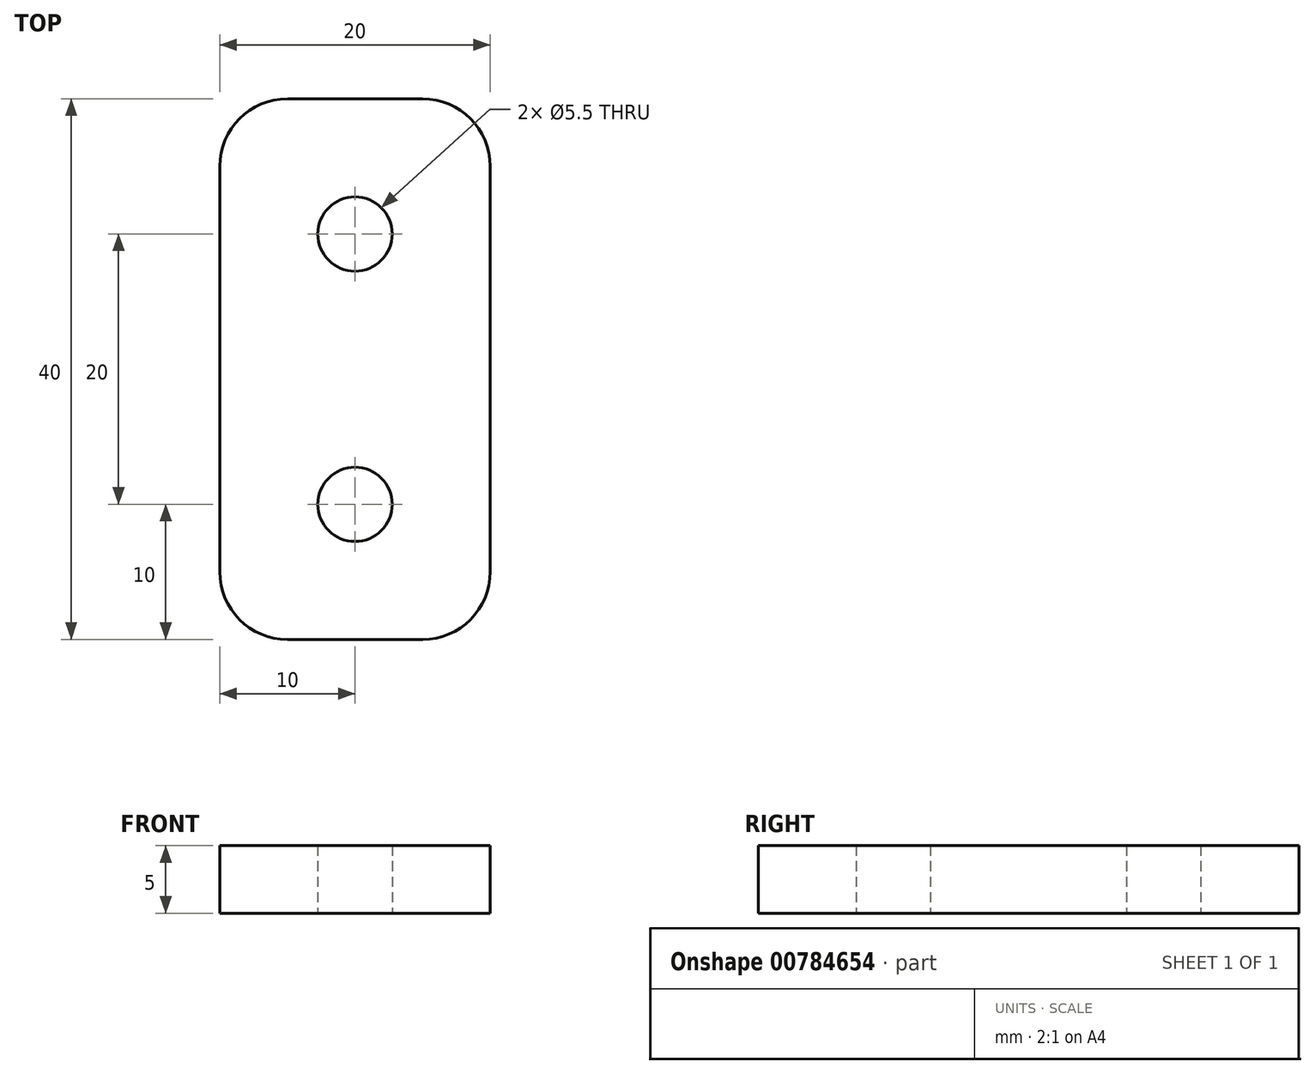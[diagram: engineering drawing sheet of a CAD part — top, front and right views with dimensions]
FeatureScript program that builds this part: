
annotation { "Feature Type Name" : "Feature", "Feature Type Description" : "" }
export const myFeature = defineFeature(function(context is Context, id is Id, definition is map)
    precondition{}
    {
        {
            var Q0;
            Q0=qCreatedBy(makeId("Top.planeOp"),FACE);
            var sketch = newSketch(context, id + "F0", { "sketchPlane" : qUnion([Q0])});
            skCircle(sketch, "E0", {"center": v(0, 10) * mm, "radius": 2.75 * mm});
            skCircle(sketch, "E1", {"center": v(0, -10) * mm, "radius": 2.75 * mm});
            skLineSegment(sketch, "E2.bottom", {"start": v(10, -20) * mm, "end": v(-10, -20) * mm});
            skLineSegment(sketch, "E2.top", {"start": v(10, 20) * mm, "end": v(-10, 20) * mm});
            skLineSegment(sketch, "E2.left", {"start": v(10, -20) * mm, "end": v(10, 20) * mm});
            skLineSegment(sketch, "E2.right", {"start": v(-10, -20) * mm, "end": v(-10, 20) * mm});
            skPoint(sketch, "E2.middle", {"position": v(0, 0) * mm});
            skSolve(sketch);
        }
        {
            var Q0;
            Q0=makeQuery(id+"F0.imprint","IMPRINT",FACE,{"disambiguationData":[TD([[makeQuery(id+"F0.imprint","IMPRINT",EDGE,{"derivedFrom":sQuery(id+"F0.wireOp",EDGE,"E0")}),-1.0]])]});
            extrude(context, id + "F1", {"entities" : qUnion([Q0]), "depth" : 5 * mm, "offsetDistance" : 25 * mm});
        }
        {
            var Q0;
            Q0=makeQuery(id+"F1.opExtrude","SWEPT_EDGE",EDGE,{"disambiguationData":[OSD([sQuery(id+"F0.wireOp",EDGE,"E2.top"),sQuery(id+"F0.wireOp",EDGE,"E2.right")])]});
            var Q1;
            Q1=makeQuery(id+"F1.opExtrude","SWEPT_EDGE",EDGE,{"disambiguationData":[OSD([sQuery(id+"F0.wireOp",EDGE,"E2.top"),sQuery(id+"F0.wireOp",EDGE,"E2.left")])]});
            var Q2;
            Q2=makeQuery(id+"F1.opExtrude","SWEPT_EDGE",EDGE,{"disambiguationData":[OSD([sQuery(id+"F0.wireOp",EDGE,"E2.bottom"),sQuery(id+"F0.wireOp",EDGE,"E2.left")])]});
            var Q3;
            Q3=makeQuery(id+"F1.opExtrude","SWEPT_EDGE",EDGE,{"disambiguationData":[OSD([sQuery(id+"F0.wireOp",EDGE,"E2.bottom"),sQuery(id+"F0.wireOp",EDGE,"E2.right")])]});
            fillet(context, id + "F2", {"entities" : qUnion([Q0, Q1, Q2, Q3]), "tangentPropagation" : true, "radius" : 5 * mm, "defaultsChanged" : false, "vertexSettings" : [], "allowEdgeOverflow" : false});
        }
    });
